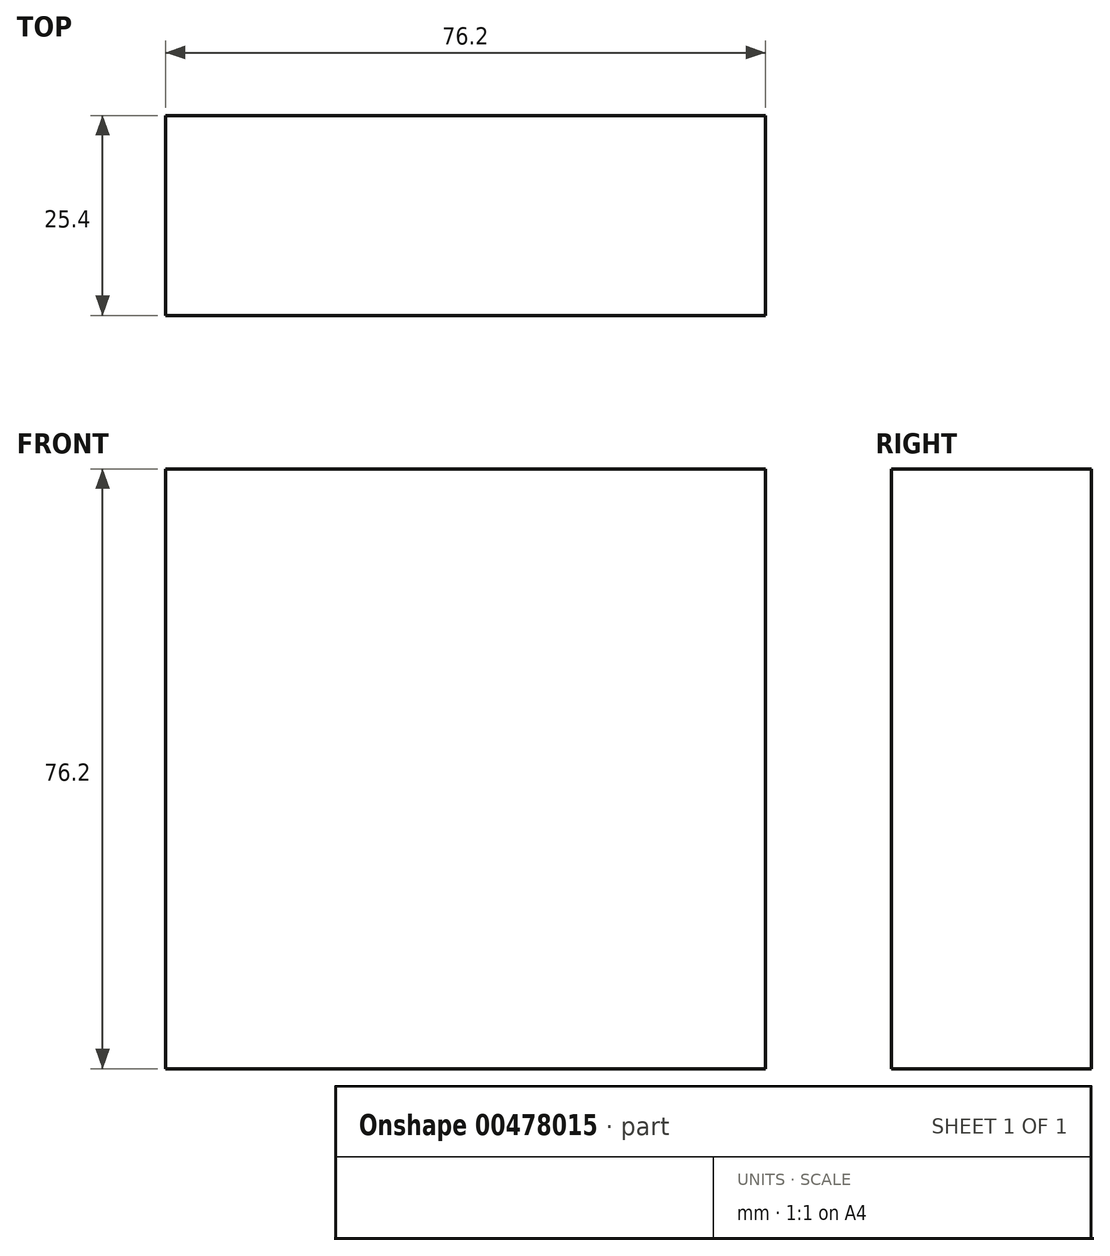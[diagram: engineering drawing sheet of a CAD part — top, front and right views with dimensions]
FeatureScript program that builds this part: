
annotation { "Feature Type Name" : "Feature", "Feature Type Description" : "" }
export const myFeature = defineFeature(function(context is Context, id is Id, definition is map)
    precondition{}
    {
        {
            var Q0;
            Q0=qCreatedBy(makeId("Front.planeOp"),FACE);
            var sketch = newSketch(context, id + "F0", { "sketchPlane" : qUnion([Q0])});
            skLineSegment(sketch, "E0.bottom", {"start": v(-39.85, 49.15) * mm, "end": v(36.35, 49.15) * mm});
            skLineSegment(sketch, "E0.top", {"start": v(-39.85, -27.05) * mm, "end": v(36.35, -27.05) * mm});
            skLineSegment(sketch, "E0.left", {"start": v(-39.85, 49.15) * mm, "end": v(-39.85, -27.05) * mm});
            skLineSegment(sketch, "E0.right", {"start": v(36.35, 49.15) * mm, "end": v(36.35, -27.05) * mm});
            skSolve(sketch);
        }
        {
            var Q0;
            Q0=makeQuery(id+"F0.imprint","IMPRINT",FACE,{"disambiguationData":[TD([[makeQuery(id+"F0.imprint","IMPRINT",EDGE,{"derivedFrom":sQuery(id+"F0.wireOp",EDGE,"E0.bottom")}),-1.0]])]});
            extrude(context, id + "F1", {"entities" : qUnion([Q0]), "depth" : 25.4 * mm});
        }
    });
